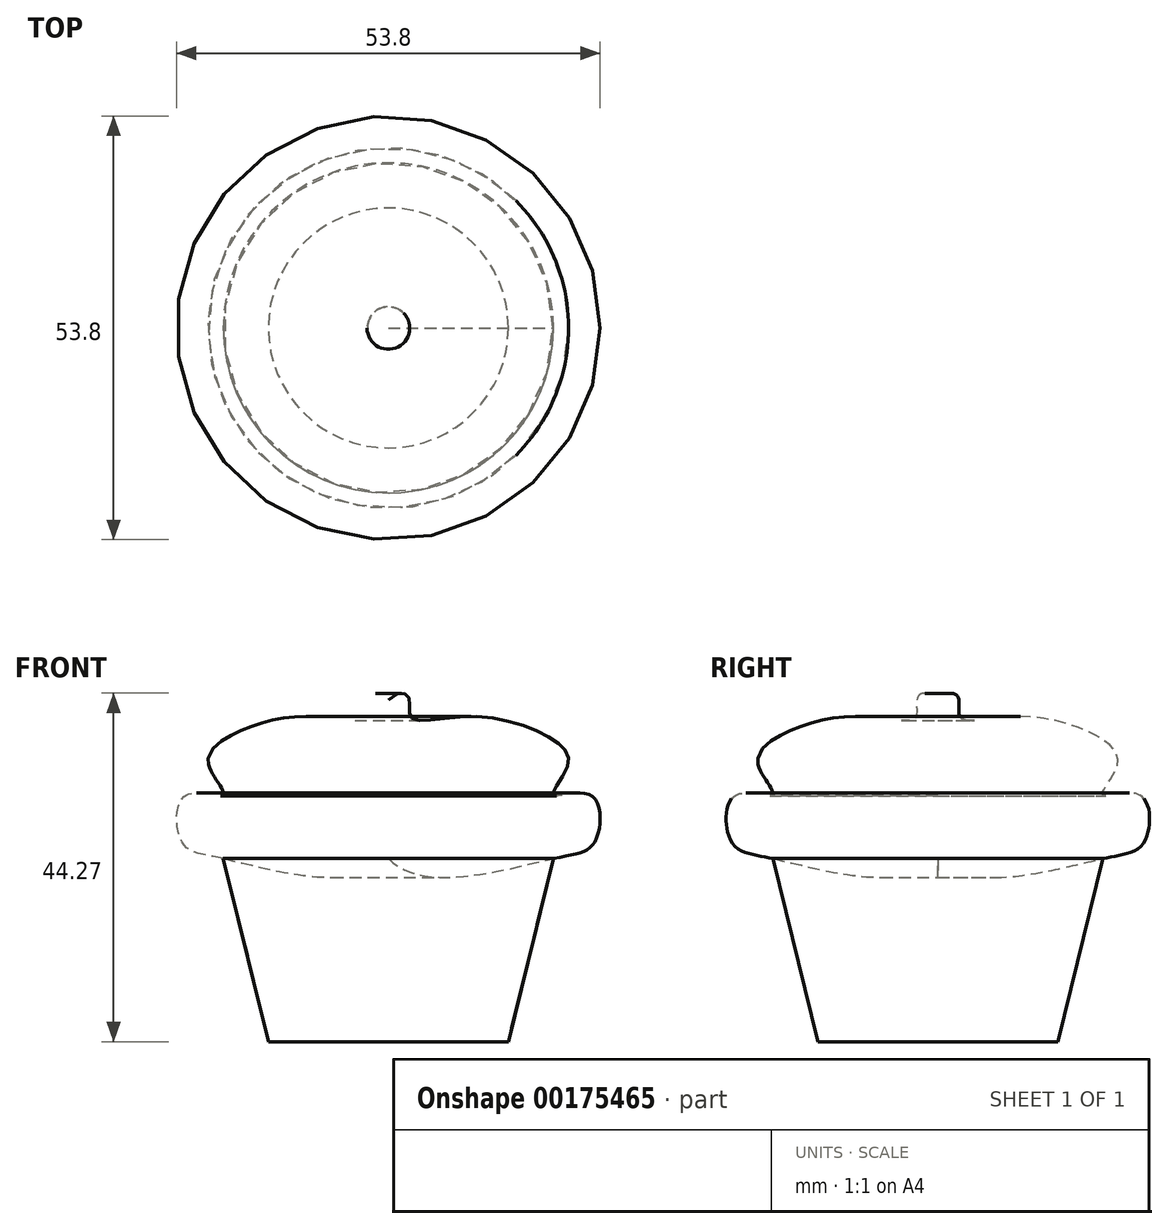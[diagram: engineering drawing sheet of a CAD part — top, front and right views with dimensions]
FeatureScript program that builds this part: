
annotation { "Feature Type Name" : "Feature", "Feature Type Description" : "" }
export const myFeature = defineFeature(function(context is Context, id is Id, definition is map)
    precondition{}
    {
        {
            var Q0;
            Q0=qCreatedBy(makeId("Front.planeOp"),FACE);
            var sketch = newSketch(context, id + "F0", { "sketchPlane" : qUnion([Q0])});
            skLineSegment(sketch, "E0", {"start": v(0, 37.76) * mm, "end": v(0, -36.18) * mm});
            skSolve(sketch);
        }
        {
            var Q0;
            Q0=qCreatedBy(makeId("Front.planeOp"),FACE);
            var sketch = newSketch(context, id + "F1", { "sketchPlane" : qUnion([Q0])});
            skLineSegment(sketch, "E1", {"start": v(0, 17.26) * mm, "end": v(20.96, 17.26) * mm});
            skLineSegment(sketch, "E2", {"start": v(20.96, 17.26) * mm, "end": v(15.24, -5.99) * mm});
            skLineSegment(sketch, "E3", {"start": v(15.24, -5.99) * mm, "end": v(0, -5.99) * mm});
            skLineSegment(sketch, "E4", {"start": v(0, -5.99) * mm, "end": v(0, 17.26) * mm});
            skFitSpline(sketch, "E5", {"points": [v(20.96, 17.26) * mm, v(26.31, 19.56) * mm, v(25.63, 25.34) * mm, v(20.96, 25.34) * mm, v(22.79, 29.08) * mm, v(20.96, 32.35) * mm, v(10.2, 35.32) * mm, v(2.86, 35.22) * mm, v(2.56, 37.78) * mm, v(0, 37.4) * mm, v(0, 17.26) * mm, v(20.96, 17.26) * mm]});
            skLineSegment(sketch, "E6", {"start": v(0, 37.4) * mm, "end": v(0, 17.26) * mm});
            skSolve(sketch);
        }
        {
            var Q0;
            {var subQ0=sQuery(id+"F1.wireOp",EDGE,"E1");Q0=makeQuery(id+"F1.imprint","IMPRINT",FACE,{"disambiguationData":[TD([[makeQuery(id+"F1.imprint","IMPRINT",EDGE,{"derivedFrom":subQ0}),1.0]])]});}
            var Q1;
            {var subQ0=sQuery(id+"F1.wireOp",EDGE,"E2");Q1=makeQuery(id+"F1.imprint","IMPRINT",FACE,{"disambiguationData":[TD([[makeQuery(id+"F1.imprint","IMPRINT",EDGE,{"derivedFrom":subQ0}),-1.0]])]});}
            var Q2;
            {var subQ0=sQuery(id+"F1.wireOp",EDGE,"E1");Q2=makeQuery(id+"F1.imprint","IMPRINT",FACE,{"disambiguationData":[TD([[makeQuery(id+"F1.imprint","IMPRINT",EDGE,{"derivedFrom":subQ0}),-1.0]])]});}
            var Q3;
            Q3=sQuery(id+"F1.wireOp",EDGE,"E4");
            revolve(context, id + "F2", {"entities" : qUnion([Q0, Q1, Q2]), "axis" : qUnion([Q3]), "revolveType" : RevolveType.FULL});
        }
        {
            var Q0;
            {var subQ0=sQuery(id+"F1.wireOp",EDGE,"E1");Q0=makeQuery(id+"F1.imprint","IMPRINT",FACE,{"disambiguationData":[TD([[makeQuery(id+"F1.imprint","IMPRINT",EDGE,{"derivedFrom":subQ0}),1.0]])]});}
            var Q1;
            {var subQ0=sQuery(id+"F1.wireOp",EDGE,"E2");Q1=makeQuery(id+"F1.imprint","IMPRINT",FACE,{"disambiguationData":[TD([[makeQuery(id+"F1.imprint","IMPRINT",EDGE,{"derivedFrom":subQ0}),-1.0]])]});}
            var Q2;
            Q2=sQuery(id+"F0.wireOp",EDGE,"E0");
            revolve(context, id + "F3", {"entities" : qUnion([Q0, Q1]), "axis" : qUnion([Q2]), "revolveType" : RevolveType.FULL});
        }
    });
